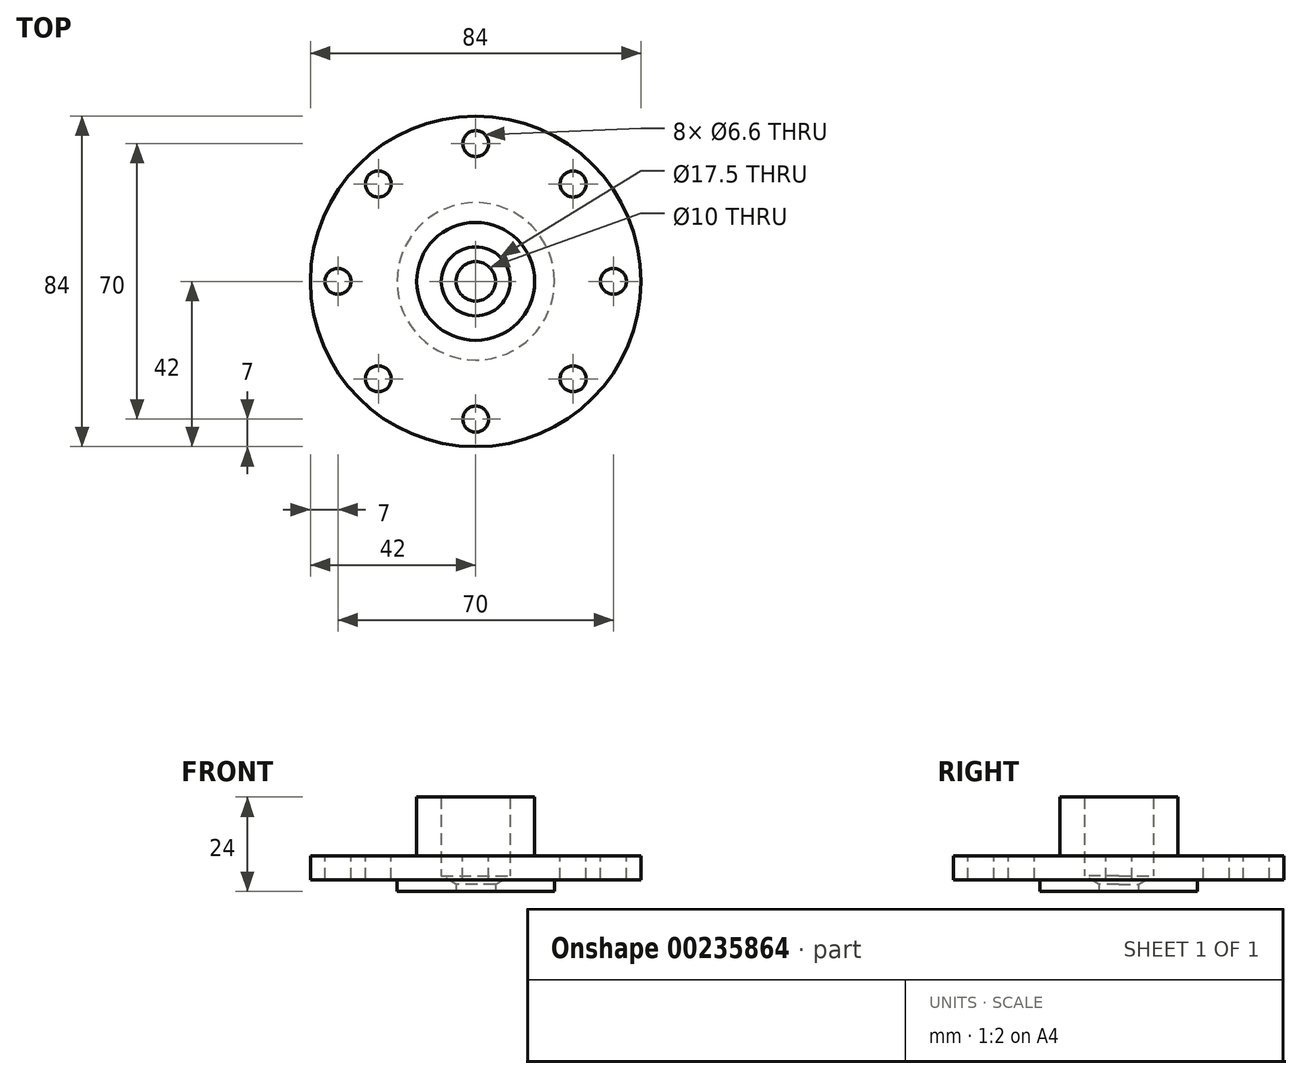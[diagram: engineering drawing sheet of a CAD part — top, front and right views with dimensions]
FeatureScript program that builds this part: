
annotation { "Feature Type Name" : "Feature", "Feature Type Description" : "" }
export const myFeature = defineFeature(function(context is Context, id is Id, definition is map)
    precondition{}
    {
        {
            var Q0;
            Q0=qCreatedBy(makeId("Top.planeOp"),FACE);
            var sketch = newSketch(context, id + "F0", { "sketchPlane" : qUnion([Q0])});
            skCircle(sketch, "E0", {"center": v(0, 0) * mm, "radius": 42 * mm});
            skCircle(sketch, "E1", {"center": v(0, 0) * mm, "radius": 35 * mm, "construction": true});
            skCircle(sketch, "E2", {"center": v(0, 0) * mm, "radius": 15 * mm});
            skLineSegment(sketch, "E3", {"start": v(0, 0) * mm, "end": v(0, 35) * mm});
            skCircle(sketch, "E4", {"center": v(0, 35) * mm, "radius": 3.3 * mm});
            skCircle(sketch, "E5.1.0", {"center": v(-24.75, 24.75) * mm, "radius": 3.3 * mm});
            skCircle(sketch, "E5.2.0", {"center": v(-35, 0) * mm, "radius": 3.3 * mm});
            skCircle(sketch, "E6.1.3.0", {"center": v(-24.75, -24.75) * mm, "radius": 3.3 * mm});
            skCircle(sketch, "E6.1.4.0", {"center": v(0, -35) * mm, "radius": 3.3 * mm});
            skCircle(sketch, "E6.1.5.0", {"center": v(24.75, -24.75) * mm, "radius": 3.3 * mm});
            skCircle(sketch, "E6.1.6.0", {"center": v(35, 0) * mm, "radius": 3.3 * mm});
            skCircle(sketch, "E6.1.7.0", {"center": v(24.75, 24.75) * mm, "radius": 3.3 * mm});
            skCircle(sketch, "E7", {"center": v(0, 0) * mm, "radius": 5 * mm, "construction": true});
            skCircle(sketch, "E8", {"center": v(0, 0) * mm, "radius": 20 * mm, "construction": true});
            skSolve(sketch);
        }
        {
            var Q0;
            Q0=makeQuery(id+"F0.imprint","IMPRINT",FACE,{"disambiguationData":[TD([[makeQuery(id+"F0.imprint","IMPRINT",EDGE,{"derivedFrom":sQuery(id+"F0.wireOp",EDGE,"E0")}),1.0]])]});
            var Q1;
            Q1=makeQuery(id+"F0.imprint","IMPRINT",FACE,{"disambiguationData":[TD([[makeQuery(id+"F0.imprint","IMPRINT",EDGE,{"derivedFrom":sQuery(id+"F0.wireOp",EDGE,"E6.1.4.0")}),1.0]])]});
            var Q2;
            Q2=makeQuery(id+"F0.imprint","IMPRINT",FACE,{"disambiguationData":[TD([[makeQuery(id+"F0.imprint","IMPRINT",EDGE,{"derivedFrom":sQuery(id+"F0.wireOp",EDGE,"E6.1.3.0")}),1.0]])]});
            var Q3;
            Q3=makeQuery(id+"F0.imprint","IMPRINT",FACE,{"disambiguationData":[TD([[makeQuery(id+"F0.imprint","IMPRINT",EDGE,{"derivedFrom":sQuery(id+"F0.wireOp",EDGE,"E5.2.0")}),1.0]])]});
            var Q4;
            Q4=makeQuery(id+"F0.imprint","IMPRINT",FACE,{"disambiguationData":[TD([[makeQuery(id+"F0.imprint","IMPRINT",EDGE,{"derivedFrom":sQuery(id+"F0.wireOp",EDGE,"E5.1.0")}),1.0]])]});
            var Q5;
            Q5=makeQuery(id+"F0.imprint","IMPRINT",FACE,{"disambiguationData":[TD([[makeQuery(id+"F0.imprint","IMPRINT",EDGE,{"derivedFrom":sQuery(id+"F0.wireOp",EDGE,"E4")}),1.0]])]});
            var Q6;
            Q6=makeQuery(id+"F0.imprint","IMPRINT",FACE,{"disambiguationData":[TD([[makeQuery(id+"F0.imprint","IMPRINT",EDGE,{"derivedFrom":sQuery(id+"F0.wireOp",EDGE,"E6.1.7.0")}),1.0]])]});
            var Q7;
            Q7=makeQuery(id+"F0.imprint","IMPRINT",FACE,{"disambiguationData":[TD([[makeQuery(id+"F0.imprint","IMPRINT",EDGE,{"derivedFrom":sQuery(id+"F0.wireOp",EDGE,"E6.1.6.0")}),1.0]])]});
            var Q8;
            Q8=makeQuery(id+"F0.imprint","IMPRINT",FACE,{"disambiguationData":[TD([[makeQuery(id+"F0.imprint","IMPRINT",EDGE,{"derivedFrom":sQuery(id+"F0.wireOp",EDGE,"E6.1.5.0")}),1.0]])]});
            extrude(context, id + "F1", {"entities" : qUnion([Q0, Q1, Q2, Q3, Q4, Q5, Q6, Q7, Q8]), "depth" : 6 * mm});
        }
        {
            var Q0;
            Q0=makeQuery(id+"F0.imprint","IMPRINT",FACE,{"disambiguationData":[TD([[makeQuery(id+"F0.imprint","IMPRINT",EDGE,{"derivedFrom":sQuery(id+"F0.wireOp",EDGE,"E2")}),1.0]])]});
            extrude(context, id + "F2", {"entities" : qUnion([Q0]), "operationType" : NewBodyOperationType.ADD, "depth" : 21 * mm});
        }
        {
            var Q0;
            Q0=qCreatedBy(makeId("Top.planeOp"),FACE);
            var sketch = newSketch(context, id + "F3", { "sketchPlane" : qUnion([Q0])});
            skCircle(sketch, "E9", {"center": v(0, 0) * mm, "radius": 20 * mm});
            skSolve(sketch);
        }
        {
            var Q0;
            Q0=makeQuery(id+"F3.imprint","IMPRINT",FACE,{"disambiguationData":[TD([[makeQuery(id+"F3.imprint","IMPRINT",EDGE,{"derivedFrom":sQuery(id+"F3.wireOp",EDGE,"E9")}),1.0]])]});
            extrude(context, id + "F4", {"entities" : qUnion([Q0]), "operationType" : NewBodyOperationType.ADD, "oppositeDirection" : true, "depth" : 3 * mm});
        }
        {
            var Q0;
            Q0=sQuery(id+"F0.wireOp",VERTEX,"E5.1.0.center");
            var Q1;
            Q1=sQuery(id+"F0.wireOp",VERTEX,"E4.center");
            var Q2;
            Q2=sQuery(id+"F0.wireOp",VERTEX,"E6.1.7.0.center");
            var Q3;
            Q3=sQuery(id+"F0.wireOp",VERTEX,"E6.1.6.0.center");
            var Q4;
            Q4=sQuery(id+"F0.wireOp",VERTEX,"E6.1.5.0.center");
            var Q5;
            Q5=sQuery(id+"F0.wireOp",VERTEX,"E6.1.4.0.center");
            var Q6;
            Q6=sQuery(id+"F0.wireOp",VERTEX,"E6.1.3.0.center");
            var Q7;
            Q7=sQuery(id+"F0.wireOp",VERTEX,"E5.2.0.center");
            var Q8;
            Q8=makeQuery(id+"F1.opExtrude","SWEPT_BODY",BODY,{"disambiguationData":[OSD([sQuery(id+"F0.wireOp",EDGE,"E0"),sQuery(id+"F0.wireOp",EDGE,"E2")])]});
            hole(context, id + "F5", {"style" : HoleStyle.C_SINK, "endStyle" : HoleEndStyle.BLIND, "oppositeDirection" : true, "holeDiameter" : 6.6 * mm, "cSinkDiameter" : 6.6 * mm, "cSinkAngle" : 90 * degree, "holeDepth" : 10 * mm, "tappedDepth" : 12 * mm, "tapClearance" : 3, "startFromSketch" : true, "locations" : qUnion([Q0, Q1, Q2, Q3, Q4, Q5, Q6, Q7]), "scope" : qUnion([Q8])});
        }
        {
            var Q0;
            Q0=qCreatedBy(makeId("Top.planeOp"),FACE);
            cPlane(context, id + "F6", {"entities" : qUnion([Q0]), "cplaneType" : CPlaneType.OFFSET, "offset" : 21 * mm, "width" : 150 * mm, "height" : 150 * mm});
        }
        {
            var Q0;
            Q0=qCreatedBy(id+"F6.planeOp",FACE);
            var sketch = newSketch(context, id + "F7", { "sketchPlane" : qUnion([Q0])});
            skCircle(sketch, "E10", {"center": v(0, 0) * mm, "radius": 8.75 * mm});
            skSolve(sketch);
        }
        {
            var Q0;
            Q0=sQuery(id+"F7.wireOp",VERTEX,"E10.center");
            var Q1;
            Q1=makeQuery(id+"F1.opExtrude","SWEPT_BODY",BODY,{"disambiguationData":[OSD([sQuery(id+"F0.wireOp",EDGE,"E0"),sQuery(id+"F0.wireOp",EDGE,"E2")])]});
            hole(context, id + "F8", {"style" : HoleStyle.C_SINK, "endStyle" : HoleEndStyle.BLIND, "holeDiameter" : 17.5 * mm, "cSinkDiameter" : 17.5 * mm, "cSinkAngle" : 90 * degree, "holeDepth" : 20 * mm, "tappedDepth" : 12 * mm, "tapClearance" : 3, "startFromSketch" : true, "locations" : qUnion([Q0]), "scope" : qUnion([Q1])});
        }
        {
            var Q0;
            Q0=qCreatedBy(makeId("Top.planeOp"),FACE);
            cPlane(context, id + "F9", {"entities" : qUnion([Q0]), "cplaneType" : CPlaneType.OFFSET, "offset" : 3 * mm, "oppositeDirection" : true, "width" : 150 * mm, "height" : 150 * mm});
        }
        {
            var Q0;
            Q0=sQuery(id+"F7.wireOp",VERTEX,"E10.center");
            var Q1;
            Q1=makeQuery(id+"F1.opExtrude","SWEPT_BODY",BODY,{"disambiguationData":[OSD([sQuery(id+"F0.wireOp",EDGE,"E0"),sQuery(id+"F0.wireOp",EDGE,"E2")])]});
            hole(context, id + "F10", {"style" : HoleStyle.SIMPLE, "endStyle" : HoleEndStyle.BLIND, "holeDiameter" : 10 * mm, "holeDepth" : 24 * mm, "tappedDepth" : 12 * mm, "tapClearance" : 3, "startFromSketch" : true, "locations" : qUnion([Q0]), "scope" : qUnion([Q1])});
        }
    });
